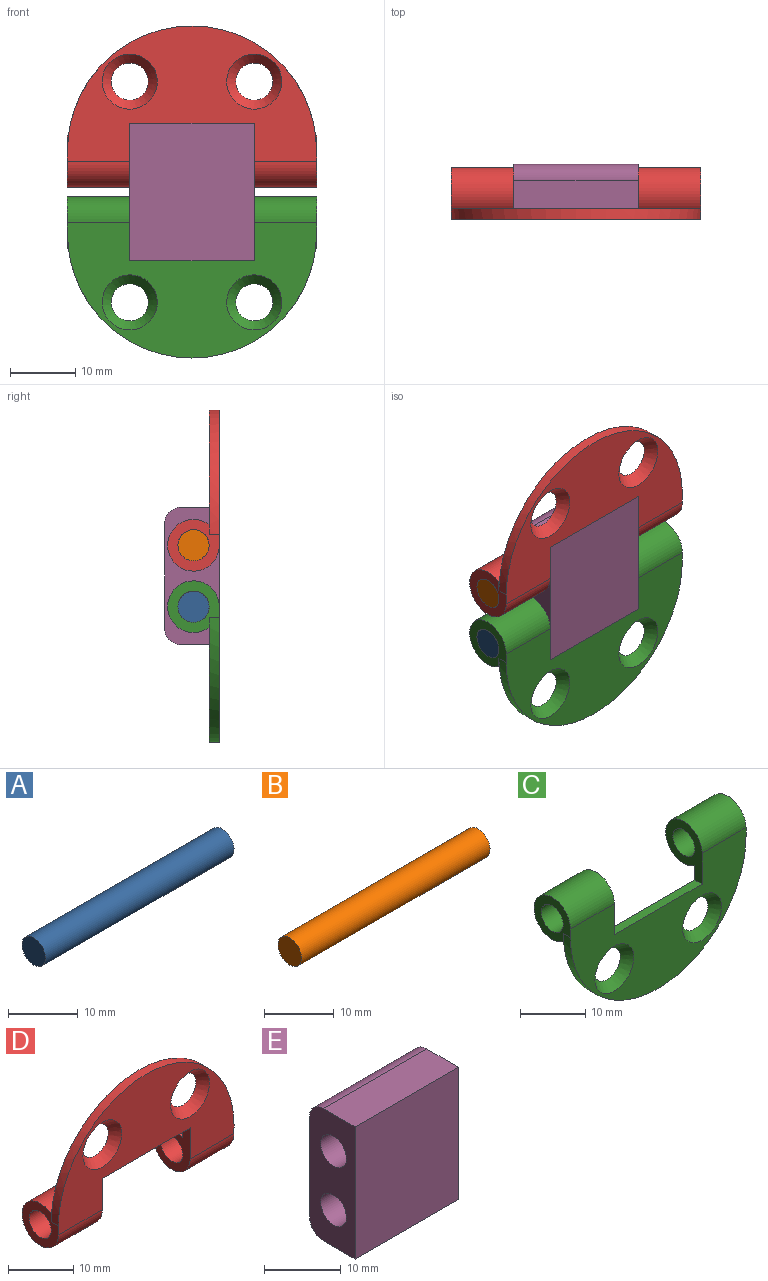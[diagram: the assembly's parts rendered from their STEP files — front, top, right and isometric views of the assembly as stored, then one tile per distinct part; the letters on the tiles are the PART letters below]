
ASSEMBLY  parts=5 mates=4
PART A: 3 faces, bbox 38.1x4.8x4.8 mm
  f0: cylinder r=2.38mm len=38.1mm, axis (-1,0,0), area 570mm2, adj f1,f2
  f1: plane 4.76x4.76mm, normal (1,0,0), area 17.8mm2, adj f0
  f2: plane 4.76x4.76mm, normal (-1,0,0), area 17.8mm2, adj f0
PART B: 3 faces, bbox 38.1x4.8x4.8 mm
  f0: cylinder r=2.38mm len=38.1mm, axis (-1,0,0), area 570mm2, adj f1,f2
  f1: plane 4.76x4.76mm, normal (1,0,0), area 17.8mm2, adj f0
  f2: plane 4.76x4.76mm, normal (-1,0,0), area 17.8mm2, adj f0
PART C: 16 faces, bbox 38.1x7.9x24.7 mm
  f0: cone r=4.22mm half-angle=41deg, axis (0,-1,0), area 46.3mm2, adj f6,f9
  f1: cone r=4.22mm half-angle=41deg, axis (0,-1,0), area 46.3mm2, adj f6,f9
  f2: cylinder r=2.38mm len=9.53mm, axis (-1,0,0), area 142.5mm2, adj f7,f12
  f3: cylinder r=3.96mm len=9.53mm, axis (-1,0,0), area 201.9mm2, adj f6,f8,f9,f11,f14
  f4: cylinder r=2.38mm len=9.53mm, axis (-1,0,0), area 142.5mm2, adj f8,f11
  f5: cylinder r=3.96mm len=9.53mm, axis (-1,0,0), area 201.9mm2, adj f6,f7,f9,f12,f13
  f6: plane 38.1x20.7mm, normal (0,-1,0), area 410mm2, adj f0,f1,f3,f5,f7,f8,f10,f11
  f7: plane 7.91x7.91mm, normal (1,0,0), area 30.5mm2, adj f2,f5,f6,f13,f15
  f8: plane 7.91x7.91mm, normal (-1,0,0), area 30.5mm2, adj f3,f4,f6,f14,f15
  f9: plane 37.98x17.54mm, normal (0,1,0), area 410.6mm2, adj f0,f1,f3,f5,f10,f11,f12,f15
  f10: plane 19.05x1.58mm, normal (0,0,1), area 30mm2, adj f6,f9,f11,f12
  f11: plane 9.8x7.91mm, normal (1,0,0), area 37.1mm2, adj f3,f4,f6,f9,f10
  f12: plane 9.8x7.91mm, normal (-1,0,0), area 37.1mm2, adj f2,f5,f6,f9,f10
  f13: plane 1.51x0.06mm, normal (0,-1,0), area 0mm2, adj f5,f7,f15
  f14: plane 1.51x0.06mm, normal (0,-1,0), area 0mm2, adj f3,f8,f15
  f15: cylinder r=19.05mm len=38.1mm, axis (0,1,0), area 94.2mm2, adj f6,f7,f8,f9,f13,f14
PART D: 16 faces, bbox 38.1x7.9x24.7 mm
  f0: cone r=4.22mm half-angle=41deg, axis (0,-1,0), area 46.3mm2, adj f7,f10
  f1: cone r=4.22mm half-angle=41deg, axis (0,-1,0), area 46.3mm2, adj f7,f10
  f2: cylinder r=19.05mm len=38.1mm, axis (0,1,0), area 94.2mm2, adj f7,f8,f9,f10,f14,f15
  f3: cylinder r=2.38mm len=9.53mm, axis (-1,0,0), area 142.5mm2, adj f9,f13
  f4: cylinder r=3.96mm len=9.53mm, axis (-1,0,0), area 201.9mm2, adj f7,f8,f10,f12,f15
  f5: cylinder r=2.38mm len=9.53mm, axis (-1,0,0), area 142.5mm2, adj f8,f12
  f6: cylinder r=3.96mm len=9.53mm, axis (-1,0,0), area 201.9mm2, adj f7,f9,f10,f13,f14
  f7: plane 38.1x20.7mm, normal (0,-1,0), area 410mm2, adj f0,f1,f2,f4,f6,f8,f9,f11
  f8: plane 7.91x7.91mm, normal (-1,0,0), area 30.5mm2, adj f2,f4,f5,f7,f15
  f9: plane 7.91x7.91mm, normal (1,0,0), area 30.5mm2, adj f2,f3,f6,f7,f14
  f10: plane 37.98x17.54mm, normal (0,1,0), area 410.6mm2, adj f0,f1,f2,f4,f6,f11,f12,f13
  f11: plane 19.05x1.58mm, normal (0,0,-1), area 30mm2, adj f7,f10,f12,f13
  f12: plane 9.8x7.91mm, normal (1,0,0), area 37.1mm2, adj f4,f5,f7,f10,f11
  f13: plane 9.8x7.91mm, normal (-1,0,0), area 37.1mm2, adj f3,f6,f7,f10,f11
  f14: plane 1.51x0.06mm, normal (0,-1,0), area 0mm2, adj f2,f6,f9
  f15: plane 1.51x0.06mm, normal (0,-1,0), area 0mm2, adj f2,f4,f8
PART E: 10 faces, bbox 19.1x8.4x21.1 mm
  f0: cylinder r=2.38mm len=19.05mm, axis (-1,0,0), area 285mm2, adj f6,f7
  f1: cylinder r=2.38mm len=19.05mm, axis (-1,0,0), area 285mm2, adj f6,f7
  f2: plane 19.05x5.84mm, normal (0,0,-1), area 111.3mm2, adj f3,f6,f7,f8
  f3: plane 21.08x19.05mm, normal (0,-1,0), area 401.6mm2, adj f2,f4,f6,f7
  f4: plane 19.05x5.84mm, normal (0,0,1), area 111.3mm2, adj f3,f6,f7,f9
  f5: plane 19.05x16mm, normal (0,1,0), area 304.8mm2, adj f6,f7,f8,f9
  f6: plane 21.08x8.38mm, normal (1,0,0), area 138.3mm2, adj f0,f1,f2,f3,f4,f5,f8,f9
  f7: plane 21.08x8.38mm, normal (-1,0,0), area 138.3mm2, adj f0,f1,f2,f3,f4,f5,f8,f9
  f8: cylinder r=2.54mm len=19.05mm, axis (-1,0,0), area 76mm2, adj f2,f5,f6,f7
  f9: cylinder r=2.54mm len=19.05mm, axis (-1,0,0), area 76mm2, adj f4,f5,f6,f7
PLACE A t=(17.72,13.13,5.22)mm
PLACE B t=(17.72,13.13,5.22)mm
PLACE C t=(17.72,13.13,5.22)mm
PLACE D t=(17.72,13.13,5.22)mm
PLACE E t=(17.72,13.13,5.22)mm fixed
MATE revolute B.f0 <-> D.f3  axis (1,0,0) through (36.77,17.09,9.92)mm
MATE revolute B.f0 <-> E.f1  axis (-1,0,0) through (17.72,17.09,9.92)mm
MATE revolute A.f0 <-> C.f2  axis (1,0,0) through (36.77,17.09,0.53)mm
MATE revolute A.f0 <-> E.f0  axis (-1,0,0) through (17.72,17.09,0.53)mm
